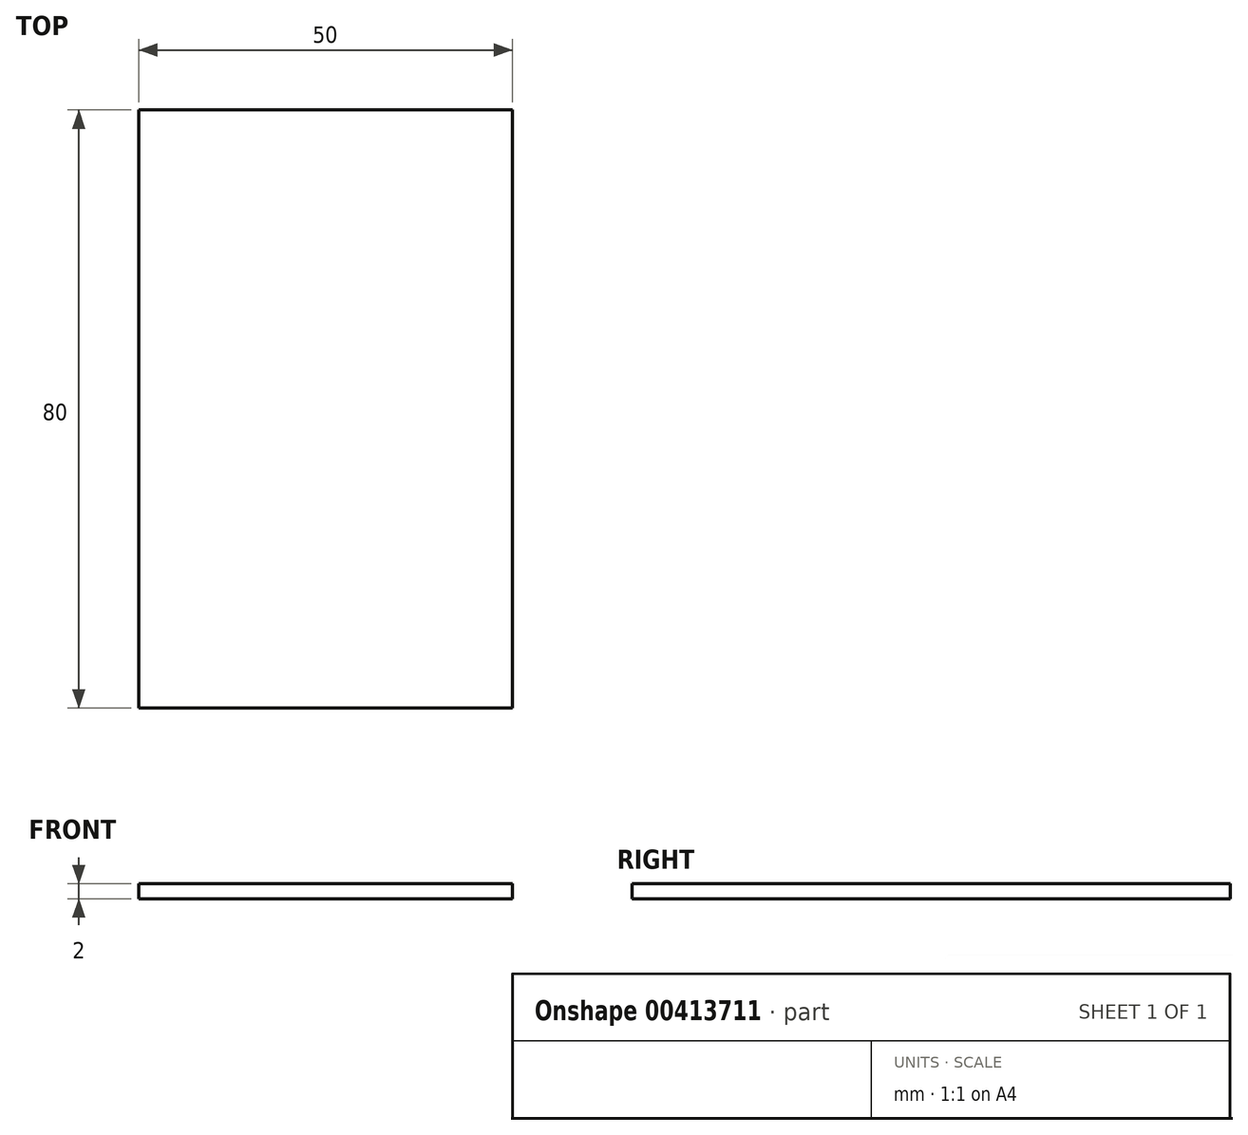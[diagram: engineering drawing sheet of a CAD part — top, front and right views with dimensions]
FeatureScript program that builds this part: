
annotation { "Feature Type Name" : "Feature", "Feature Type Description" : "" }
export const myFeature = defineFeature(function(context is Context, id is Id, definition is map)
    precondition{}
    {
        {
            var Q0;
            Q0=qCreatedBy(makeId("Top.planeOp"),FACE);
            var sketch = newSketch(context, id + "F0", { "sketchPlane" : qUnion([Q0])});
            skLineSegment(sketch, "E0.bottom", {"start": v(1.47, 0) * mm, "end": v(-48.53, 0) * mm});
            skLineSegment(sketch, "E0.top", {"start": v(1.47, 80) * mm, "end": v(-48.53, 80) * mm});
            skLineSegment(sketch, "E0.left", {"start": v(1.47, 0) * mm, "end": v(1.47, 80) * mm});
            skLineSegment(sketch, "E0.right", {"start": v(-48.53, 0) * mm, "end": v(-48.53, 80) * mm});
            skSolve(sketch);
        }
        {
            var Q0;
            Q0 = qSketchRegion(id + "F0", true);
            extrude(context, id + "F1", {"entities" : qUnion([Q0]), "depth" : 2 * mm});
        }
    });
